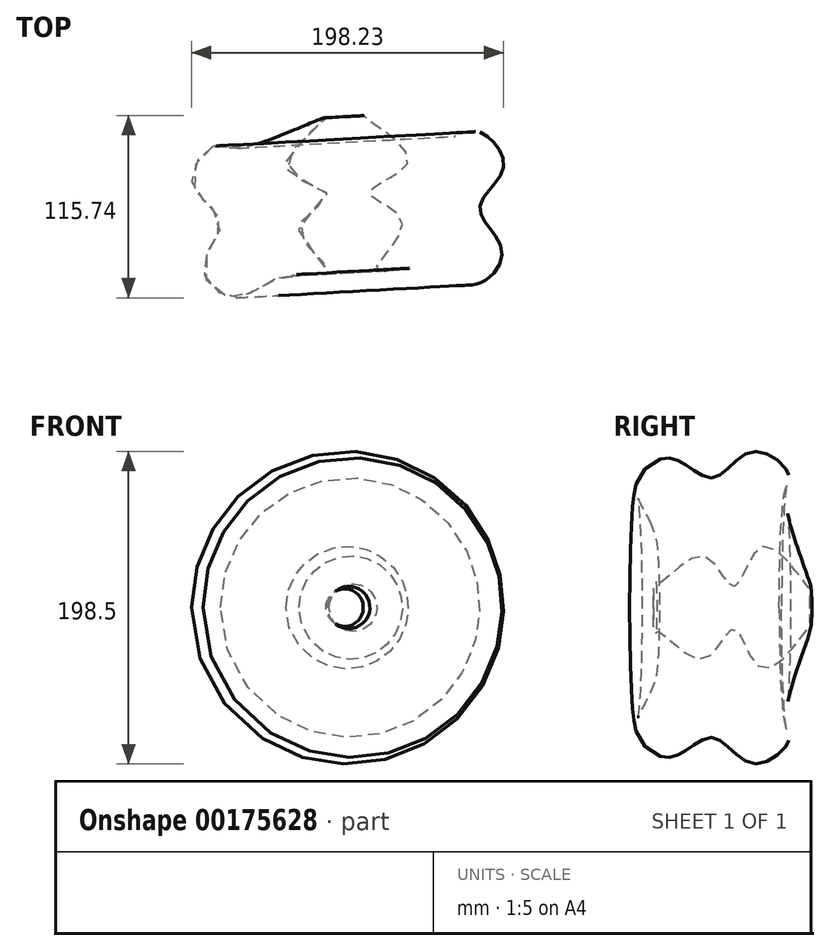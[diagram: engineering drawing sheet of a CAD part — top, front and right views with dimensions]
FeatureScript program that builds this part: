
annotation { "Feature Type Name" : "Feature", "Feature Type Description" : "" }
export const myFeature = defineFeature(function(context is Context, id is Id, definition is map)
    precondition{}
    {
        {
            var Q0;
            Q0=qCreatedBy(makeId("Top.planeOp"),FACE);
            var sketch = newSketch(context, id + "F0", { "sketchPlane" : qUnion([Q0])});
            skFitSpline(sketch, "E0", {"points": [v(-32.8, 45.21) * mm, v(-45.35, 21.82) * mm, v(-27.38, -2.42) * mm, v(-38.5, -31.52) * mm, v(-18.26, -50.63) * mm, v(12.27, -36.94) * mm, v(41.65, -33.52) * mm, v(22.53, -5.85) * mm, v(40.79, 14.98) * mm, v(14.26, 32.95) * mm, v(39.65, 63.47) * mm, v(-14.26, 44.64) * mm, v(-32.8, 45.21) * mm]});
            skLineSegment(sketch, "E1", {"start": v(52.48, 46.64) * mm, "end": v(57.05, -36.65) * mm});
            skSolve(sketch);
        }
        {
            var Q0;
            Q0 = qSketchRegion(id + "F0", true);
            var Q1;
            Q1=sQuery(id+"F0.wireOp",EDGE,"E1");
            revolve(context, id + "F1", {"entities" : qUnion([Q0]), "axis" : qUnion([Q1]), "revolveType" : RevolveType.FULL});
        }
    });
